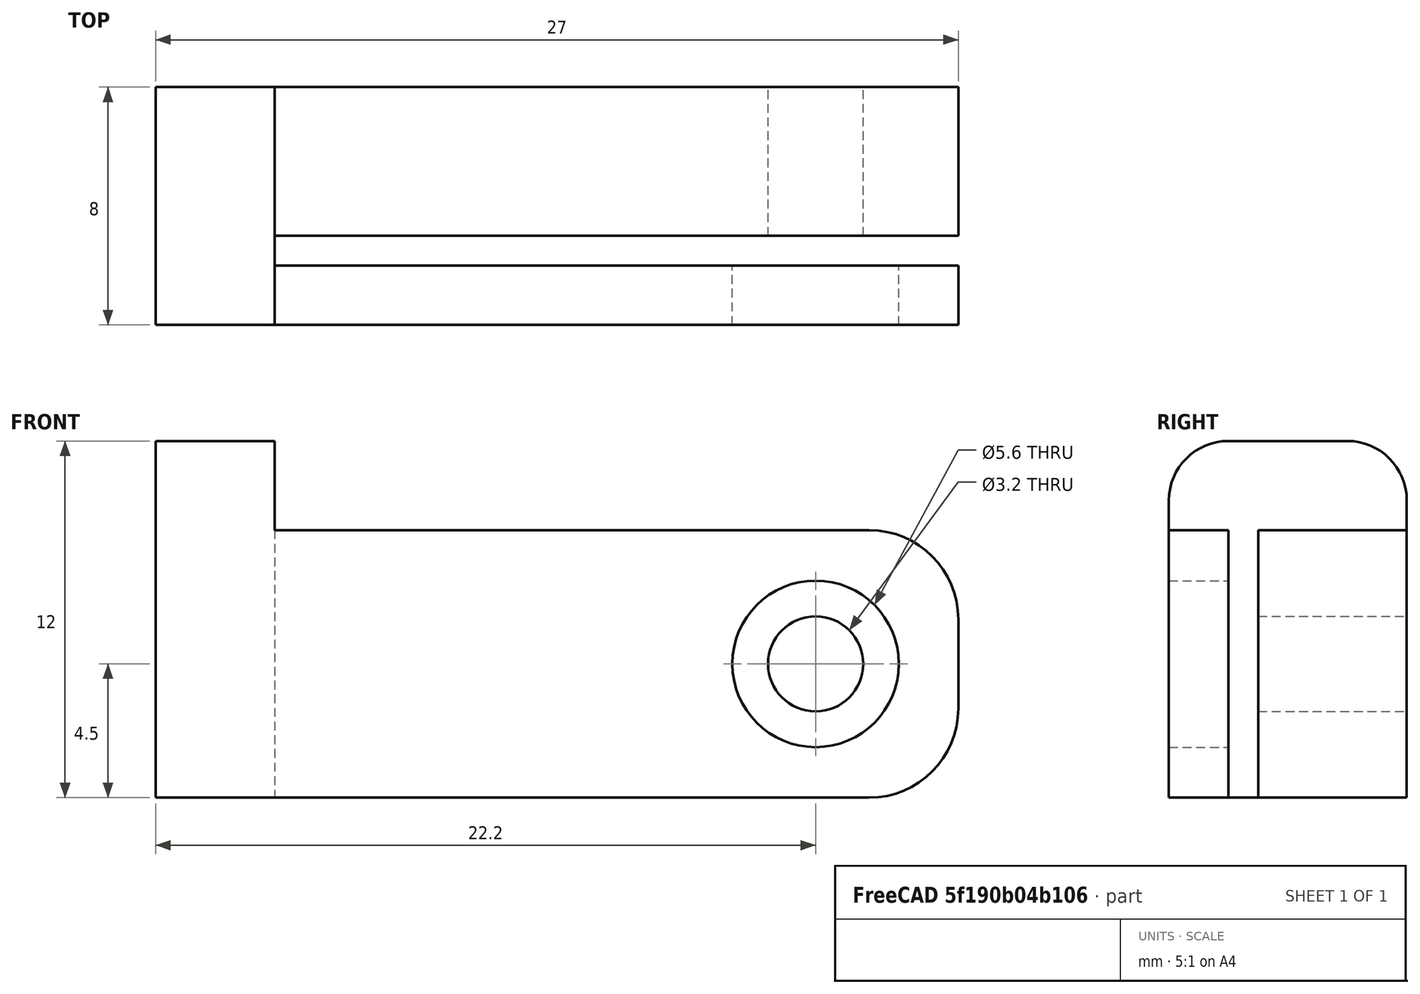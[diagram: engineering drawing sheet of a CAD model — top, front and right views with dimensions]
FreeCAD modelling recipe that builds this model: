
FCSTD DOCUMENT  (FreeCAD 0.19R)
Label: power_socker_screw_connector
License: All rights reserved
LicenseURL: http://en.wikipedia.org/wiki/All_rights_reserved
objects: Part::Box×3, Part::Fillet×3, Part::Cylinder×2, Part::Cut×2, Part::MultiFuse×1
note: 11 computed .brp shape members not serialized (recipe doc carries the construction recipe); baked Part::Feature solids carry a one-line shape summary decoded from their .brp

FEATURE [Part::Box] Box  label="front plate"
  AttacherType = Attacher::AttachEngine3D
  Height = 9
  Length = 27
  Width = 2
FEATURE [Part::Box] Box001  label="back plate"
  AttacherType = Attacher::AttachEngine3D
  Height = 9
  Length = 27
  Placement = pos=(0,3,0) rot=(0,0,1;0rad)
  Width = 5
  expr: .Placement.Base.y = <<front plate>>.Width + 1mm
  expr: Height = <<front plate>>.Height
  expr: Length = <<front plate>>.Length
FEATURE [Part::Box] Box002  label="glue cube"
  AttacherType = Attacher::AttachEngine3D
  Height = 12
  Length = 4
  Width = 8
  expr: Width = <<back plate>>.Placement.Base.y + <<back plate>>.Width
FEATURE [Part::Cylinder] Cylinder  label="pass hole"
  Angle = 360
  AttacherType = Attacher::AttachEngine3D
  Height = 2
  Placement = pos=(22.2,0,4.5) rot=(1,0,0;4.71239rad)
  Radius = 2.8
  expr: .Placement.Base.x = <<front plate>>.Length - 2mm - Radius
  expr: .Placement.Base.z = <<front plate>>.Height / 2
  expr: Height = <<front plate>>.Width
FEATURE [Part::Cylinder] Cylinder001  label="screw hole"
  Angle = 360
  AttacherType = Attacher::AttachEngine3D
  Height = 5
  Placement = pos=(22.2,3,4.5) rot=(-1,0,0;1.5708rad)
  Radius = 1.6
  expr: .Placement.Base.y = <<back plate>>.Placement.Base.y
  expr: Height = <<back plate>>.Width
  expr: .Placement.Base.z = <<front plate>>.Height / 2
  expr: .Placement.Base.x = <<front plate>>.Length - 2mm - <<pass hole>>.Radius
FEATURE [Part::Fillet] Fillet  label="back plate fillet"
  Base = -> Box001
  Edges = 2 edges r=3: [Edge6,Edge8]
FEATURE [Part::Cut] Cut001  label="back cut"
  Base = -> Fillet
  Tool = -> Cylinder001
FEATURE [Part::Fillet] Fillet001  label="front plate fillet"
  Base = -> Box
  Edges = 2 edges r=3: [Edge6,Edge8]
FEATURE [Part::Cut] Cut  label="front cut"
  Base = -> Fillet001
  Tool = -> Cylinder
FEATURE [Part::Fillet] Fillet002  label="glue cube fillet"
  Base = -> Box002
  Edges = 2 edges r=2: [Edge10,Edge12]
FEATURE [Part::MultiFuse] Fusion  label="power socket screw connector"
  Shapes = -> [Cut,Cut001,Fillet002]
